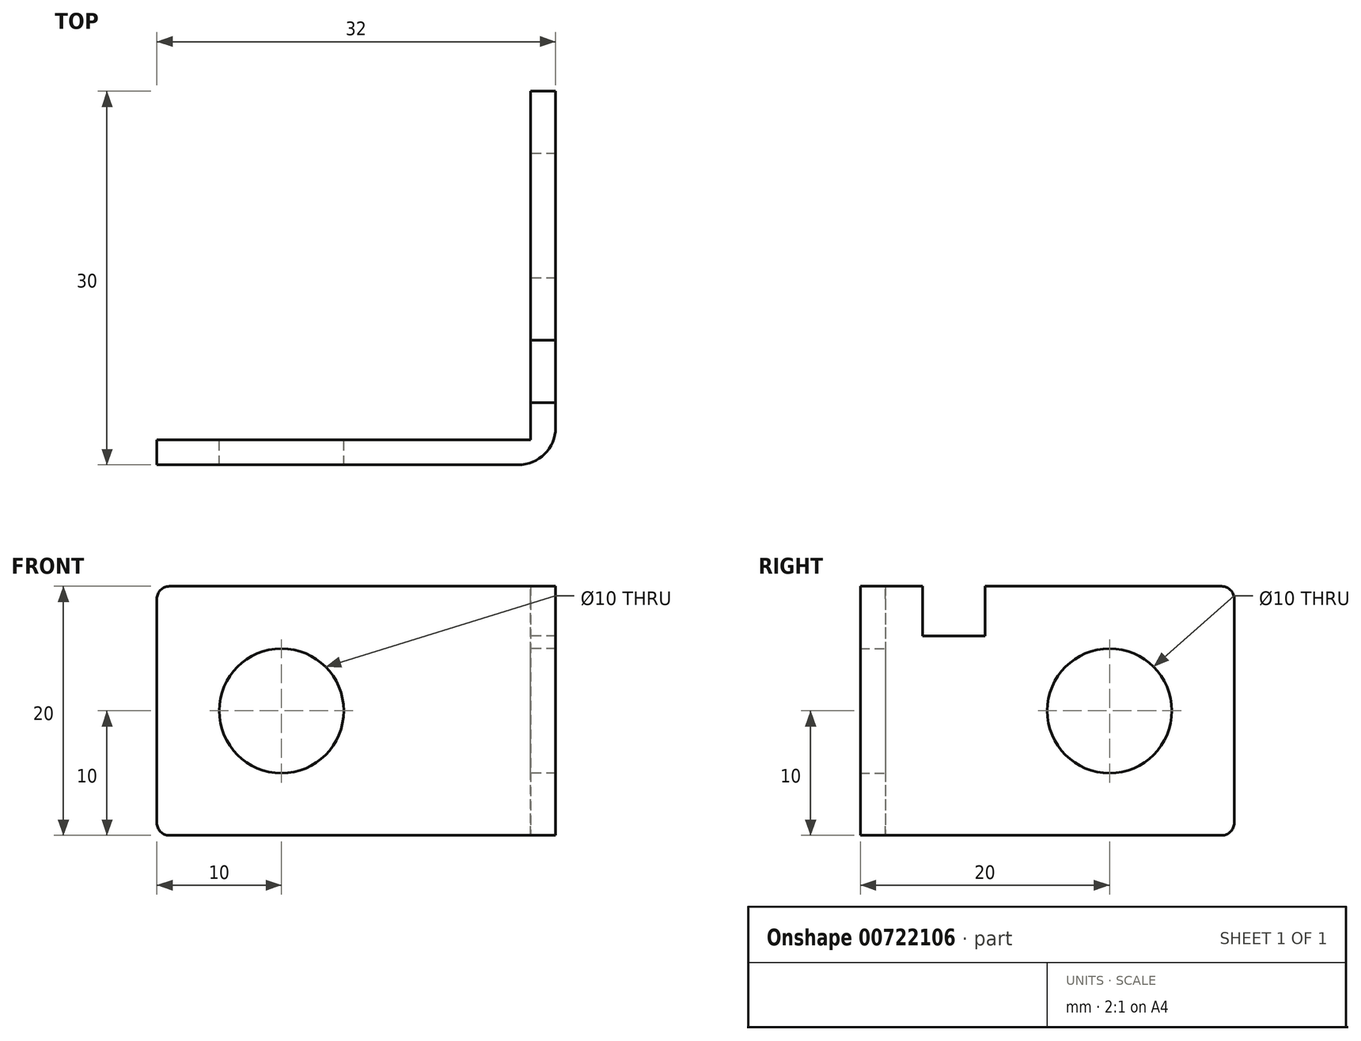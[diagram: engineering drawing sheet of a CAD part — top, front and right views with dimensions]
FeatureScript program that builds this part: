
annotation { "Feature Type Name" : "Feature", "Feature Type Description" : "" }
export const myFeature = defineFeature(function(context is Context, id is Id, definition is map)
    precondition{}
    {
        {
            var Q0;
            Q0=qCreatedBy(makeId("Right.planeOp"),FACE);
            var sketch = newSketch(context, id + "F0", { "sketchPlane" : qUnion([Q0])});
            skLineSegment(sketch, "E0", {"start": v(0, 0) * mm, "end": v(0, 20) * mm});
            skLineSegment(sketch, "E1", {"start": v(0, 20) * mm, "end": v(2, 20) * mm});
            skLineSegment(sketch, "E2", {"start": v(2, 20) * mm, "end": v(2, 0) * mm});
            skLineSegment(sketch, "E3", {"start": v(2, 0) * mm, "end": v(0, 0) * mm});
            skSolve(sketch);
        }
        {
            var Q0;
            Q0 = qSketchRegion(id + "F0", true);
            extrude(context, id + "F1", {"entities" : qUnion([Q0]), "depth" : 30 * mm, "offsetDistance" : 25 * mm});
        }
        {
            var Q0;
            Q0=makeQuery(id+"F1.opExtrude","SWEPT_FACE",FACE,{"disambiguationData":[OSD([sQuery(id+"F0.wireOp",EDGE,"E2")])]});
            var sketch = newSketch(context, id + "F2", { "sketchPlane" : qUnion([Q0])});
            skCircle(sketch, "E4", {"center": v(-10, 10) * mm, "radius": 5 * mm});
            skSolve(sketch);
        }
        {
            var Q0;
            Q0 = qSketchRegion(id + "F2", true);
            extrude(context, id + "F3", {"entities" : qUnion([Q0]), "operationType" : NewBodyOperationType.REMOVE, "oppositeDirection" : true, "depth" : 2 * mm, "offsetDistance" : 25 * mm});
        }
        {
            var Q0;
            Q0=makeQuery(id+"F1.opExtrude","CAP_FACE",FACE,{"disambiguationData":[OSD([sQuery(id+"F0.wireOp",EDGE,"E0"),sQuery(id+"F0.wireOp",EDGE,"E1"),sQuery(id+"F0.wireOp",EDGE,"E2"),sQuery(id+"F0.wireOp",EDGE,"E3")])],"isStart":false});
            var sketch = newSketch(context, id + "F4", { "sketchPlane" : qUnion([Q0])});
            skLineSegment(sketch, "E5", {"start": v(0, 0) * mm, "end": v(30, 0) * mm});
            skLineSegment(sketch, "E6", {"start": v(30, 0) * mm, "end": v(30, 20) * mm});
            skCircle(sketch, "E7", {"center": v(20, 10) * mm, "radius": 5 * mm});
            skLineSegment(sketch, "E8", {"start": v(0, 20) * mm, "end": v(0, 0) * mm});
            skLineSegment(sketch, "E9", {"start": v(30, 20) * mm, "end": v(10, 20) * mm});
            skLineSegment(sketch, "E10", {"start": v(10, 20) * mm, "end": v(10, 16) * mm});
            skLineSegment(sketch, "E11", {"start": v(10, 16) * mm, "end": v(5, 16) * mm});
            skLineSegment(sketch, "E12", {"start": v(5, 16) * mm, "end": v(5, 20) * mm});
            skLineSegment(sketch, "E13", {"start": v(5, 20) * mm, "end": v(0, 20) * mm});
            skSolve(sketch);
        }
        {
            var Q0;
            Q0 = qSketchRegion(id + "F4", true);
            extrude(context, id + "F5", {"entities" : qUnion([Q0]), "operationType" : NewBodyOperationType.ADD, "depth" : 2 * mm, "offsetDistance" : 25 * mm});
        }
        {
            var Q0;
            Q0=makeQuery(id+"F1.opExtrude","CAP_EDGE",EDGE,{"disambiguationData":[OSD([sQuery(id+"F0.wireOp",EDGE,"E2")])],"isStart":false});
            var Q1;
            Q1=makeQuery(id+"F5.opExtrude","SWEPT_EDGE",EDGE,{"disambiguationData":[OSD([sQuery(id+"F4.wireOp",EDGE,"E6"),sQuery(id+"F4.wireOp",EDGE,"IuPikUZ2-MfNm-7qNP-2wKQ-IpGCOwYoF46Y")])]});
            var Q2;
            Q2=makeQuery(id+"F5.opExtrude","SWEPT_EDGE",EDGE,{"disambiguationData":[OSD([sQuery(id+"F4.wireOp",EDGE,"E5"),sQuery(id+"F4.wireOp",EDGE,"E6")])]});
            var Q3;
            Q3=makeQuery(id+"F1.opExtrude","CAP_EDGE",EDGE,{"disambiguationData":[OSD([sQuery(id+"F0.wireOp",EDGE,"E1")])],"isStart":true});
            var Q4;
            Q4=makeQuery(id+"F1.opExtrude","CAP_EDGE",EDGE,{"disambiguationData":[OSD([sQuery(id+"F0.wireOp",EDGE,"E3")])],"isStart":true});
            fillet(context, id + "F6", {"entities" : qUnion([Q0, Q1, Q2, Q3, Q4]), "radius" : 1 * mm, "tangentPropagation" : true, "allowEdgeOverflow" : false});
        }
        {
            var Q0;
            Q0=makeQuery(id+"F5.opExtrude","CAP_EDGE",EDGE,{"disambiguationData":[OSD([sQuery(id+"F4.wireOp",EDGE,"E8")])],"isStart":false});
            fillet(context, id + "F7", {"entities" : qUnion([Q0]), "radius" : 3 * mm, "tangentPropagation" : true, "allowEdgeOverflow" : false});
        }
    });
